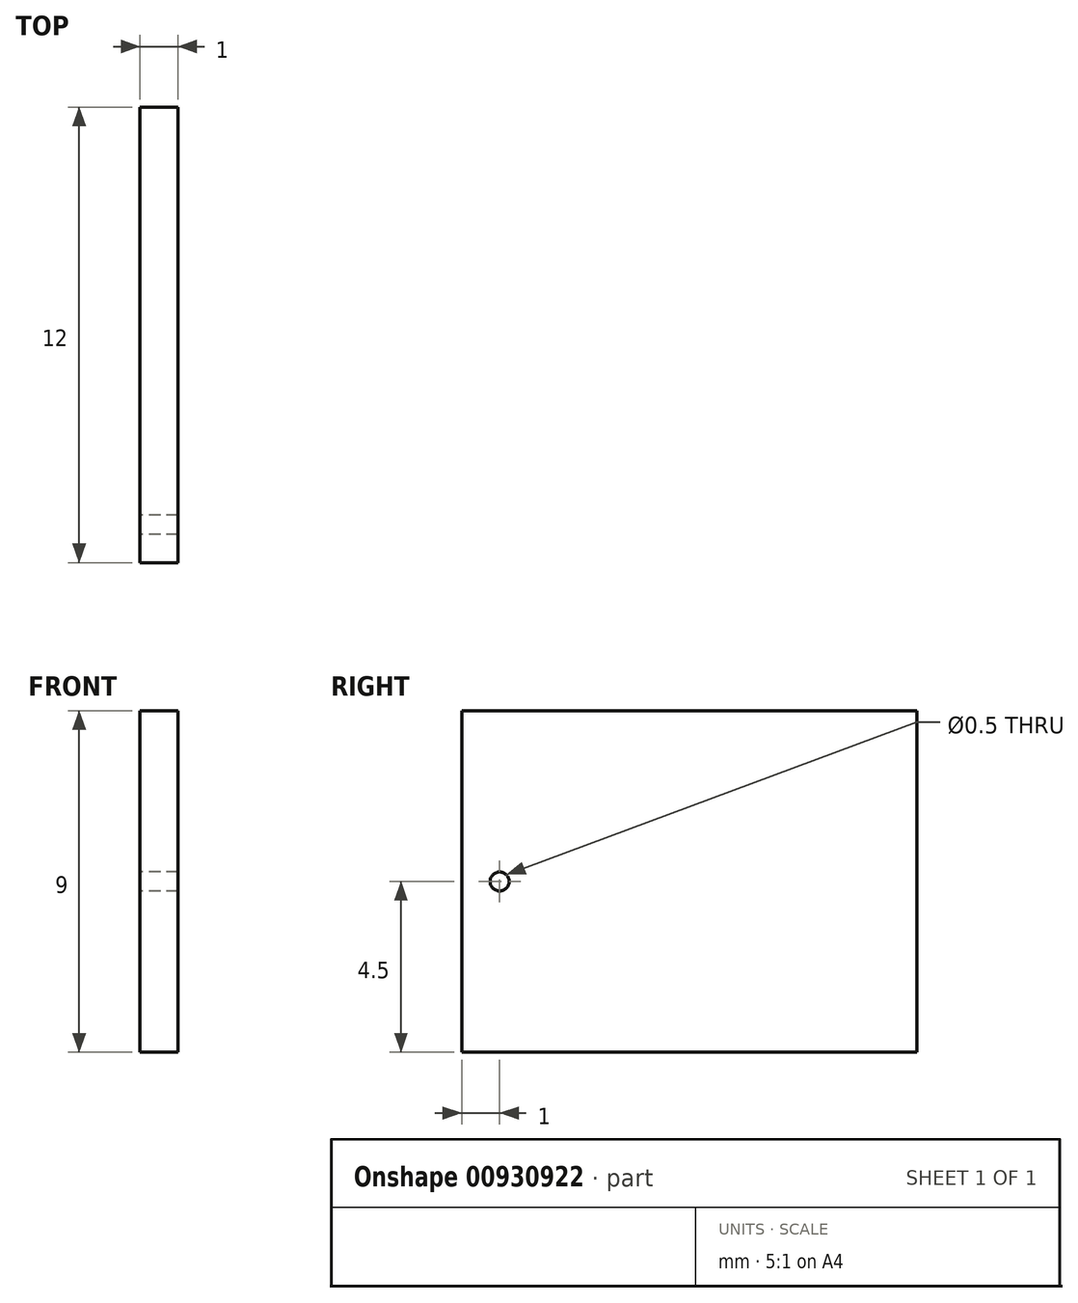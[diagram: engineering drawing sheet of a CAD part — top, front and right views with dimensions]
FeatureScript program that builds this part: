
annotation { "Feature Type Name" : "Feature", "Feature Type Description" : "" }
export const myFeature = defineFeature(function(context is Context, id is Id, definition is map)
    precondition{}
    {
        {
            var Q0;
            Q0=qCreatedBy(makeId("Right.planeOp"),FACE);
            var sketch = newSketch(context, id + "F0", { "sketchPlane" : qUnion([Q0])});
            skLineSegment(sketch, "E0.bottom", {"start": v(6, 4.5) * mm, "end": v(-6, 4.5) * mm});
            skLineSegment(sketch, "E0.top", {"start": v(6, -4.5) * mm, "end": v(-6, -4.5) * mm});
            skLineSegment(sketch, "E0.left", {"start": v(6, 4.5) * mm, "end": v(6, -4.5) * mm});
            skLineSegment(sketch, "E0.right", {"start": v(-6, 4.5) * mm, "end": v(-6, -4.5) * mm});
            skPoint(sketch, "E0.middle", {"position": v(0, 0) * mm});
            skCircle(sketch, "E1", {"center": v(-5, 0) * mm, "radius": 0.25 * mm});
            skSolve(sketch);
        }
        {
            var Q0;
            Q0=makeQuery(id+"F0.imprint","IMPRINT",FACE,{"disambiguationData":[TD([[makeQuery(id+"F0.imprint","IMPRINT",EDGE,{"derivedFrom":sQuery(id+"F0.wireOp",EDGE,"E0.bottom")}),1.0]])]});
            extrude(context, id + "F1", {"entities" : qUnion([Q0]), "depth" : 1 * mm, "offsetDistance" : 25 * mm});
        }
    });
